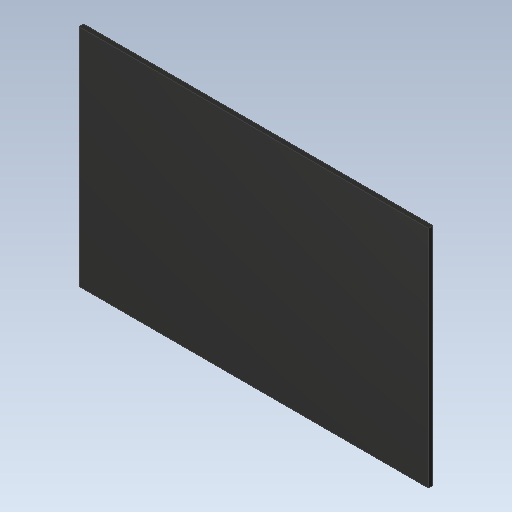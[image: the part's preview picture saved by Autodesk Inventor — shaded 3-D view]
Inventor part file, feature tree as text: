
AUTODESK INVENTOR PART (.ipt)
format: ipt  version: 2020 (Build 240168000, 168)  size: 86,016 bytes
history: imported  units: in
note: dims shown in document units (in); Inventor stores cm internally (conversion verified against a paired STEP export)
features: imported_body x1
ambient origin geometry x8: Origin, YZ Plane, XZ Plane, XY Plane, X Axis, Y Axis, Z Axis, Center Point
bodies: Solid1 (imported_parasolid), Body1 (imported_parasolid)
feature tree (1):
  imported_body  NMx_Import_Brep_tag  [imported B-rep: ~6 faces, bbox_mm=[7.6952, 4.953, 0.1]]
